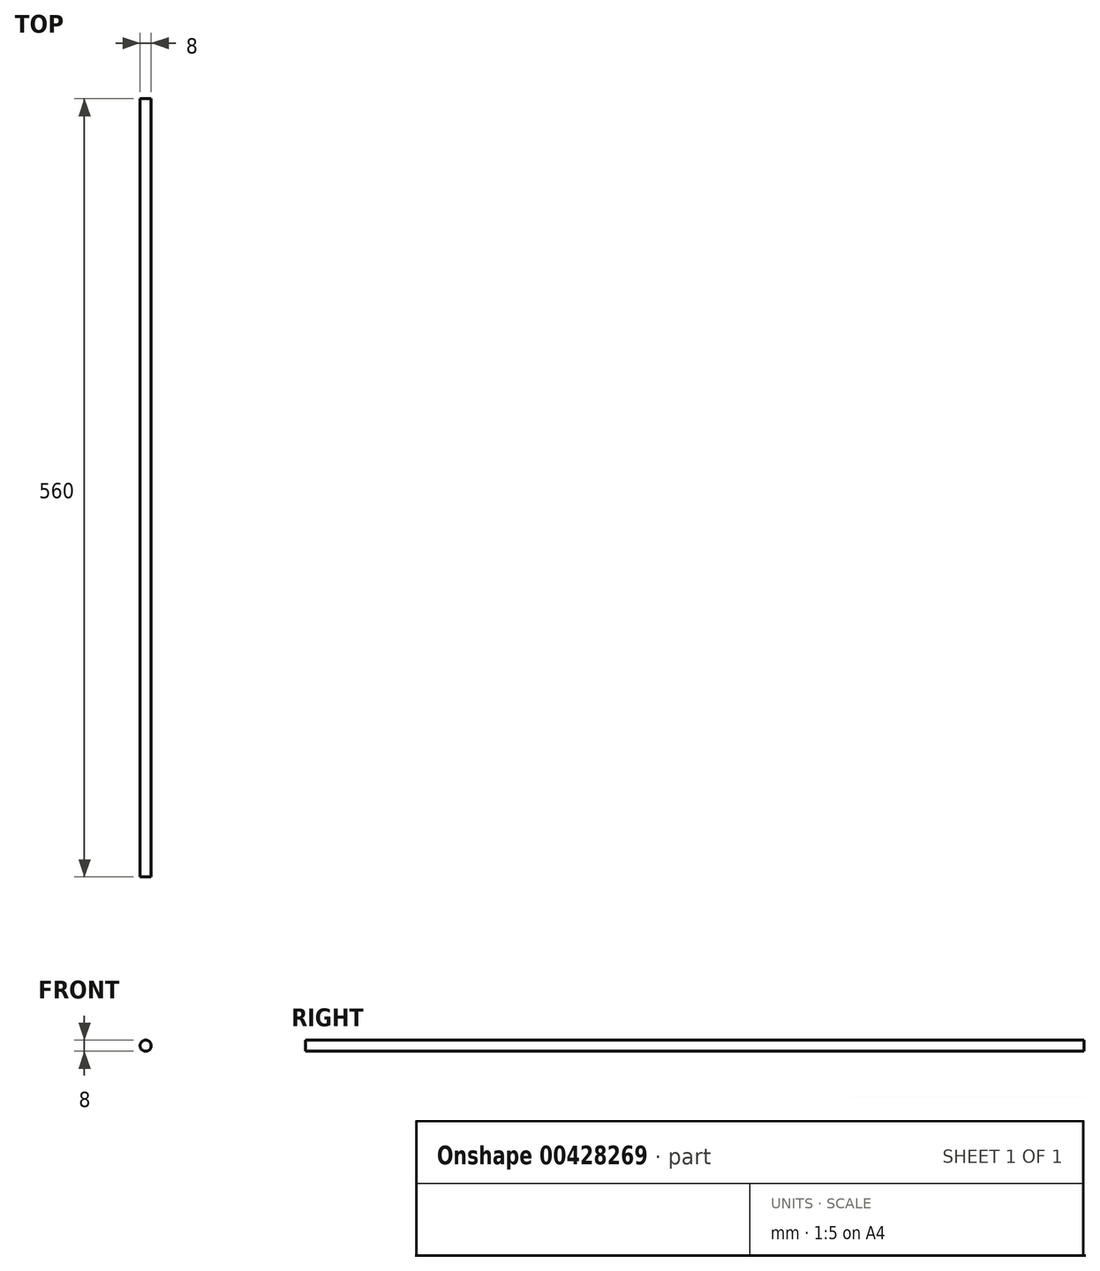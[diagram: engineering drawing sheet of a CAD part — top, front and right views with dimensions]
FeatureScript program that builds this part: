
annotation { "Feature Type Name" : "Feature", "Feature Type Description" : "" }
export const myFeature = defineFeature(function(context is Context, id is Id, definition is map)
    precondition{}
    {
        {
            var Q0;
            Q0=qCreatedBy(makeId("Front.planeOp"),FACE);
            var sketch = newSketch(context, id + "F0", { "sketchPlane" : qUnion([Q0])});
            skCircle(sketch, "E0", {"center": v(0, 0) * mm, "radius": 4 * mm});
            skSolve(sketch);
        }
        {
            var Q0;
            Q0=makeQuery(id+"F0.imprint","IMPRINT",FACE,{"disambiguationData":[TD([[makeQuery(id+"F0.imprint","IMPRINT",EDGE,{"derivedFrom":sQuery(id+"F0.wireOp",EDGE,"E0")}),1.0]])]});
            extrude(context, id + "F1", {"entities" : qUnion([Q0]), "depth" : 560 * mm, "symmetric" : true});
        }
    });
